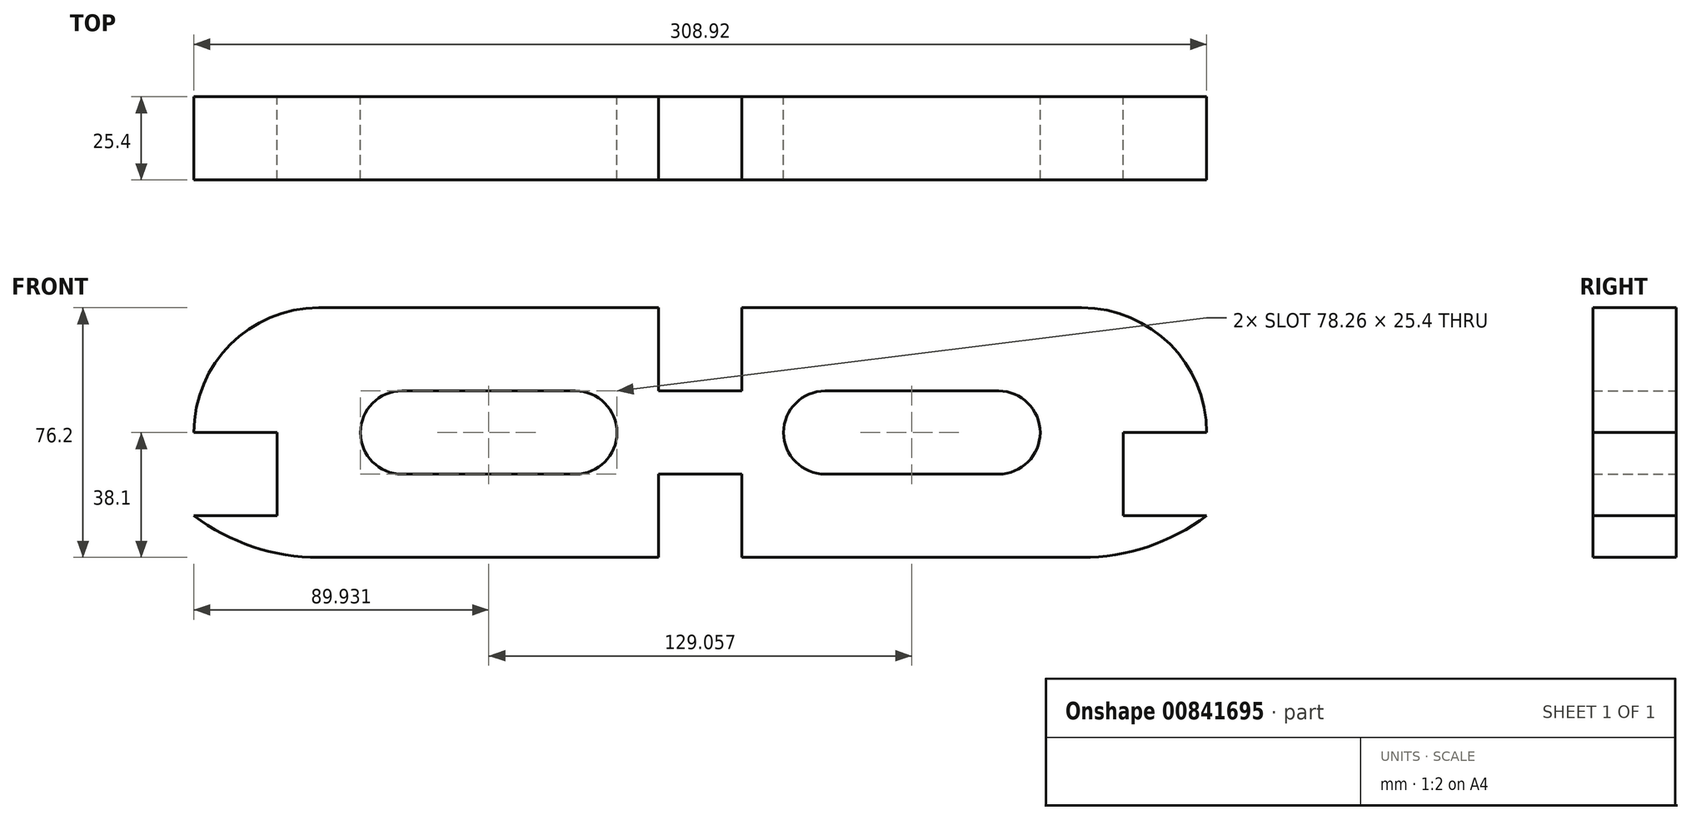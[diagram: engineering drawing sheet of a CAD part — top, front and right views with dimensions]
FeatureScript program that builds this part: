
annotation { "Feature Type Name" : "Feature", "Feature Type Description" : "" }
export const myFeature = defineFeature(function(context is Context, id is Id, definition is map)
    precondition{}
    {
        {
            var Q0;
            Q0=qCreatedBy(makeId("Front.planeOp"),FACE);
            var sketch = newSketch(context, id + "F0", { "sketchPlane" : qUnion([Q0])});
            skLineSegment(sketch, "E0", {"start": v(0, 0) * mm, "end": v(-129.06, 0) * mm, "construction": true});
            skLineSegment(sketch, "E1", {"start": v(-129.06, 12.7) * mm, "end": v(-129.06, -12.7) * mm});
            skLineSegment(sketch, "E2", {"start": v(0, 0) * mm, "end": v(0, 50.8) * mm, "construction": true});
            skLineSegment(sketch, "E3", {"start": v(0, 50.8) * mm, "end": v(-116.36, 50.8) * mm});
            skLineSegment(sketch, "E4", {"start": v(-129.06, 12.7) * mm, "end": v(-154.46, 12.7) * mm});
            skLineSegment(sketch, "E5", {"start": v(-129.06, -12.7) * mm, "end": v(-129.06, -12.7) * mm});
            skLineSegment(sketch, "E6", {"start": v(-129.06, -12.7) * mm, "end": v(-154.46, -12.7) * mm});
            skArc(sketch, "E7", {"start": v(-116.36, 50.8) * mm, "mid": v(-143.3, 39.64) * mm, "end": v(-154.46, 12.7) * mm});
            skLineSegment(sketch, "E8", {"start": v(-154.46, 12.7) * mm, "end": v(-154.46, -12.7) * mm, "construction": true});
            skLineSegment(sketch, "E9", {"start": v(0, 0) * mm, "end": v(0, -25.4) * mm, "construction": true});
            skLineSegment(sketch, "E10", {"start": v(0, -25.4) * mm, "end": v(-116.36, -25.4) * mm});
            skLineSegment(sketch, "E11", {"start": v(-116.36, 50.8) * mm, "end": v(-116.36, -25.4) * mm, "construction": true});
            skArc(sketch, "E12", {"start": v(-154.46, -12.7) * mm, "mid": v(-136.44, -22.14) * mm, "end": v(-116.36, -25.4) * mm});
            skLineSegment(sketch, "E13", {"start": v(-90.96, 25.4) * mm, "end": v(-38.1, 25.4) * mm});
            skLineSegment(sketch, "E14", {"start": v(-25.4, 12.7) * mm, "end": v(-25.4, 12.7) * mm});
            skLineSegment(sketch, "E15", {"start": v(-38.1, 0) * mm, "end": v(-90.96, 0) * mm});
            skLineSegment(sketch, "E16", {"start": v(-103.66, 12.7) * mm, "end": v(-103.66, 12.7) * mm});
            skPoint(sketch, "E17.visualSharp", {"position": v(-103.66, 25.4) * mm});
            skArc(sketch, "E17.filletArc", {"start": v(-90.96, 25.4) * mm, "mid": v(-99.94, 21.68) * mm, "end": v(-103.66, 12.7) * mm});
            skPoint(sketch, "E18.visualSharp", {"position": v(-103.66, 0) * mm});
            skArc(sketch, "E18.filletArc", {"start": v(-103.66, 12.7) * mm, "mid": v(-99.94, 3.72) * mm, "end": v(-90.96, 0) * mm});
            skPoint(sketch, "E19.visualSharp", {"position": v(-25.4, 25.4) * mm});
            skArc(sketch, "E19.filletArc", {"start": v(-25.4, 12.7) * mm, "mid": v(-29.12, 21.68) * mm, "end": v(-38.1, 25.4) * mm});
            skPoint(sketch, "E20.visualSharp", {"position": v(-25.4, 0) * mm});
            skArc(sketch, "E20.filletArc", {"start": v(-38.1, 0) * mm, "mid": v(-29.12, 3.72) * mm, "end": v(-25.4, 12.7) * mm});
            skLineSegment(sketch, "E21.MirrorCS", {"start": v(0, 50.8) * mm, "end": v(116.36, 50.8) * mm});
            skArc(sketch, "E22.MirrorCS", {"start": v(116.36, 50.8) * mm, "mid": v(143.3, 39.64) * mm, "end": v(154.46, 12.7) * mm});
            skLineSegment(sketch, "E23.MirrorCS", {"start": v(129.06, 12.7) * mm, "end": v(154.46, 12.7) * mm});
            skLineSegment(sketch, "E24.MirrorCS", {"start": v(129.06, 12.7) * mm, "end": v(129.06, -12.7) * mm});
            skLineSegment(sketch, "E25.MirrorCS", {"start": v(129.06, -12.7) * mm, "end": v(154.46, -12.7) * mm});
            skArc(sketch, "E26.MirrorCS", {"start": v(154.46, -12.7) * mm, "mid": v(136.44, -22.14) * mm, "end": v(116.36, -25.4) * mm});
            skLineSegment(sketch, "E27.MirrorCS", {"start": v(0, -25.4) * mm, "end": v(116.36, -25.4) * mm});
            skLineSegment(sketch, "E28.MirrorCS", {"start": v(0, 0) * mm, "end": v(129.06, 0) * mm, "construction": true});
            skLineSegment(sketch, "E29.MirrorCS", {"start": v(90.96, 25.4) * mm, "end": v(38.1, 25.4) * mm});
            skArc(sketch, "E30.MirrorCS", {"start": v(103.66, 12.7) * mm, "mid": v(99.94, 3.72) * mm, "end": v(90.96, 0) * mm});
            skArc(sketch, "E31.MirrorCS", {"start": v(90.96, 25.4) * mm, "mid": v(99.94, 21.68) * mm, "end": v(103.66, 12.7) * mm});
            skArc(sketch, "E32.MirrorCS", {"start": v(38.1, 0) * mm, "mid": v(29.12, 3.72) * mm, "end": v(25.4, 12.7) * mm});
            skArc(sketch, "E33.MirrorCS", {"start": v(25.4, 12.7) * mm, "mid": v(29.12, 21.68) * mm, "end": v(38.1, 25.4) * mm});
            skLineSegment(sketch, "E34", {"start": v(38.1, 0) * mm, "end": v(90.96, 0) * mm});
            skSolve(sketch);
        }
        {
            var Q0;
            Q0 = qSketchRegion(id + "F0", true);
            extrude(context, id + "F1", {"entities" : qUnion([Q0]), "depth" : 25.4 * mm, "offsetDistance" : 25.4 * mm});
        }
        {
            var Q0;
            Q0=makeQuery(id+"F1.opExtrude","CAP_FACE",FACE,{"disambiguationData":[OSD([sQuery(id+"F0.wireOp",EDGE,"E1"),sQuery(id+"F0.wireOp",EDGE,"E3"),sQuery(id+"F0.wireOp",EDGE,"E4"),sQuery(id+"F0.wireOp",EDGE,"E6"),sQuery(id+"F0.wireOp",EDGE,"E7"),sQuery(id+"F0.wireOp",EDGE,"E10"),sQuery(id+"F0.wireOp",EDGE,"E12"),sQuery(id+"F0.wireOp",EDGE,"E13"),sQuery(id+"F0.wireOp",EDGE,"E15"),sQuery(id+"F0.wireOp",EDGE,"E17.filletArc"),sQuery(id+"F0.wireOp",EDGE,"E18.filletArc"),sQuery(id+"F0.wireOp",EDGE,"E19.filletArc"),sQuery(id+"F0.wireOp",EDGE,"E20.filletArc"),sQuery(id+"F0.wireOp",EDGE,"E21.MirrorCS"),sQuery(id+"F0.wireOp",EDGE,"E22.MirrorCS"),sQuery(id+"F0.wireOp",EDGE,"E23.MirrorCS"),sQuery(id+"F0.wireOp",EDGE,"E24.MirrorCS"),sQuery(id+"F0.wireOp",EDGE,"E25.MirrorCS"),sQuery(id+"F0.wireOp",EDGE,"E26.MirrorCS"),sQuery(id+"F0.wireOp",EDGE,"E27.MirrorCS"),sQuery(id+"F0.wireOp",EDGE,"E29.MirrorCS"),sQuery(id+"F0.wireOp",EDGE,"E30.MirrorCS"),sQuery(id+"F0.wireOp",EDGE,"E31.MirrorCS"),sQuery(id+"F0.wireOp",EDGE,"E32.MirrorCS"),sQuery(id+"F0.wireOp",EDGE,"E33.MirrorCS"),sQuery(id+"F0.wireOp",EDGE,"E34")])],"isStart":false});
            var sketch = newSketch(context, id + "F2", { "sketchPlane" : qUnion([Q0])});
            skLineSegment(sketch, "E35.bottom", {"start": v(-12.7, 50.8) * mm, "end": v(12.7, 50.8) * mm});
            skLineSegment(sketch, "E35.top", {"start": v(-12.7, 25.4) * mm, "end": v(12.7, 25.4) * mm});
            skLineSegment(sketch, "E35.left", {"start": v(-12.7, 50.8) * mm, "end": v(-12.7, 25.4) * mm});
            skLineSegment(sketch, "E35.right", {"start": v(12.7, 50.8) * mm, "end": v(12.7, 25.4) * mm});
            skLineSegment(sketch, "E36.bottom", {"start": v(-12.7, -25.4) * mm, "end": v(12.7, -25.4) * mm});
            skLineSegment(sketch, "E36.top", {"start": v(-12.7, 0) * mm, "end": v(12.7, 0) * mm});
            skLineSegment(sketch, "E36.left", {"start": v(-12.7, -25.4) * mm, "end": v(-12.7, 0) * mm});
            skLineSegment(sketch, "E36.right", {"start": v(12.7, -25.4) * mm, "end": v(12.7, 0) * mm});
            skLineSegment(sketch, "E37", {"start": v(0, 0) * mm, "end": v(0, 25.4) * mm, "construction": true});
            skSolve(sketch);
        }
        {
            var Q0;
            Q0 = qSketchRegion(id + "F2", true);
            extrude(context, id + "F3", {"entities" : qUnion([Q0]), "operationType" : NewBodyOperationType.REMOVE, "oppositeDirection" : true, "depth" : 25.4 * mm, "offsetDistance" : 25.4 * mm});
        }
    });
